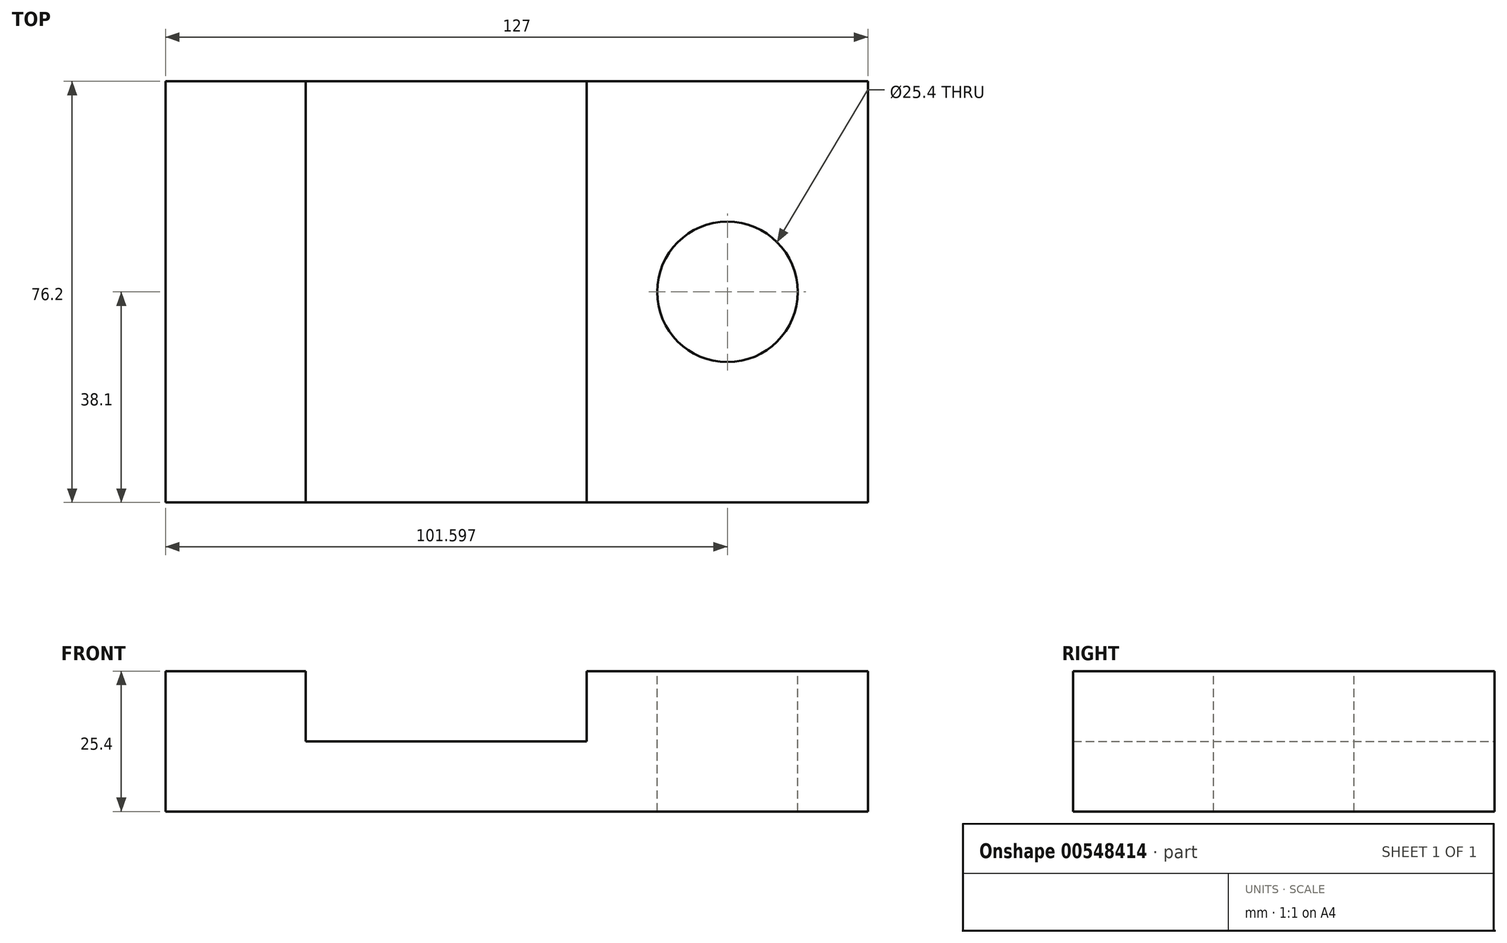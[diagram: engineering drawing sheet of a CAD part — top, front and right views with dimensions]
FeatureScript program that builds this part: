
annotation { "Feature Type Name" : "Feature", "Feature Type Description" : "" }
export const myFeature = defineFeature(function(context is Context, id is Id, definition is map)
    precondition{}
    {
        {
            var Q0;
            Q0=qCreatedBy(makeId("Front.planeOp"),FACE);
            var sketch = newSketch(context, id + "F0", { "sketchPlane" : qUnion([Q0])});
            skLineSegment(sketch, "E0", {"start": v(-51.96, -39.31) * mm, "end": v(-51.96, -64.71) * mm});
            skLineSegment(sketch, "E1", {"start": v(-51.96, -64.71) * mm, "end": v(75.04, -64.71) * mm});
            skLineSegment(sketch, "E2", {"start": v(75.04, -64.71) * mm, "end": v(75.04, -39.31) * mm});
            skLineSegment(sketch, "E3", {"start": v(75.04, -39.31) * mm, "end": v(24.22, -39.31) * mm});
            skLineSegment(sketch, "E4", {"start": v(24.22, -39.31) * mm, "end": v(24.22, -52.01) * mm});
            skLineSegment(sketch, "E5", {"start": v(24.22, -52.01) * mm, "end": v(-26.58, -52.01) * mm});
            skLineSegment(sketch, "E6", {"start": v(-26.58, -52.01) * mm, "end": v(-26.58, -39.31) * mm});
            skLineSegment(sketch, "E7", {"start": v(-26.58, -39.31) * mm, "end": v(-51.96, -39.31) * mm});
            skLineSegment(sketch, "E8", {"start": v(36.93, -39.31) * mm, "end": v(36.93, -64.71) * mm});
            skLineSegment(sketch, "E9", {"start": v(62.33, -39.31) * mm, "end": v(62.33, -64.71) * mm});
            skSolve(sketch);
        }
        {
            var Q0;
            Q0 = qSketchRegion(id + "F0", true);
            extrude(context, id + "F1", {"entities" : qUnion([Q0]), "depth" : 76.2 * mm, "offsetDistance" : 25.4 * mm});
        }
        {
            var Q0;
            Q0=makeQuery(id+"F1.opExtrude","SWEPT_FACE",FACE,{"disambiguationData":[OSD([sQuery(id+"F0.wireOp",EDGE,"E3")])]});
            var sketch = newSketch(context, id + "F2", { "sketchPlane" : qUnion([Q0])});
            skCircle(sketch, "E10", {"center": v(49.64, -38.1) * mm, "radius": 12.7 * mm});
            skSolve(sketch);
        }
        {
            var Q0;
            Q0=sQuery(id+"F2.wireOp",VERTEX,"E10.center");
            var Q1;
            Q1=makeQuery(id+"F1.opExtrude","SWEPT_BODY",BODY,{"disambiguationData":[OSD([sQuery(id+"F0.wireOp",EDGE,"E0"),sQuery(id+"F0.wireOp",EDGE,"E1"),sQuery(id+"F0.wireOp",EDGE,"E2"),sQuery(id+"F0.wireOp",EDGE,"E3"),sQuery(id+"F0.wireOp",EDGE,"E4"),sQuery(id+"F0.wireOp",EDGE,"E5"),sQuery(id+"F0.wireOp",EDGE,"E6"),sQuery(id+"F0.wireOp",EDGE,"E7")])]});
            hole(context, id + "F3", {"style" : HoleStyle.SIMPLE, "endStyle" : HoleEndStyle.THROUGH, "holeDiameter" : 25.4 * mm, "isTappedThrough" : true, "tappedDepth" : 12.7 * mm, "tapClearance" : 3, "locations" : qUnion([Q0]), "scope" : qUnion([Q1])});
        }
    });
